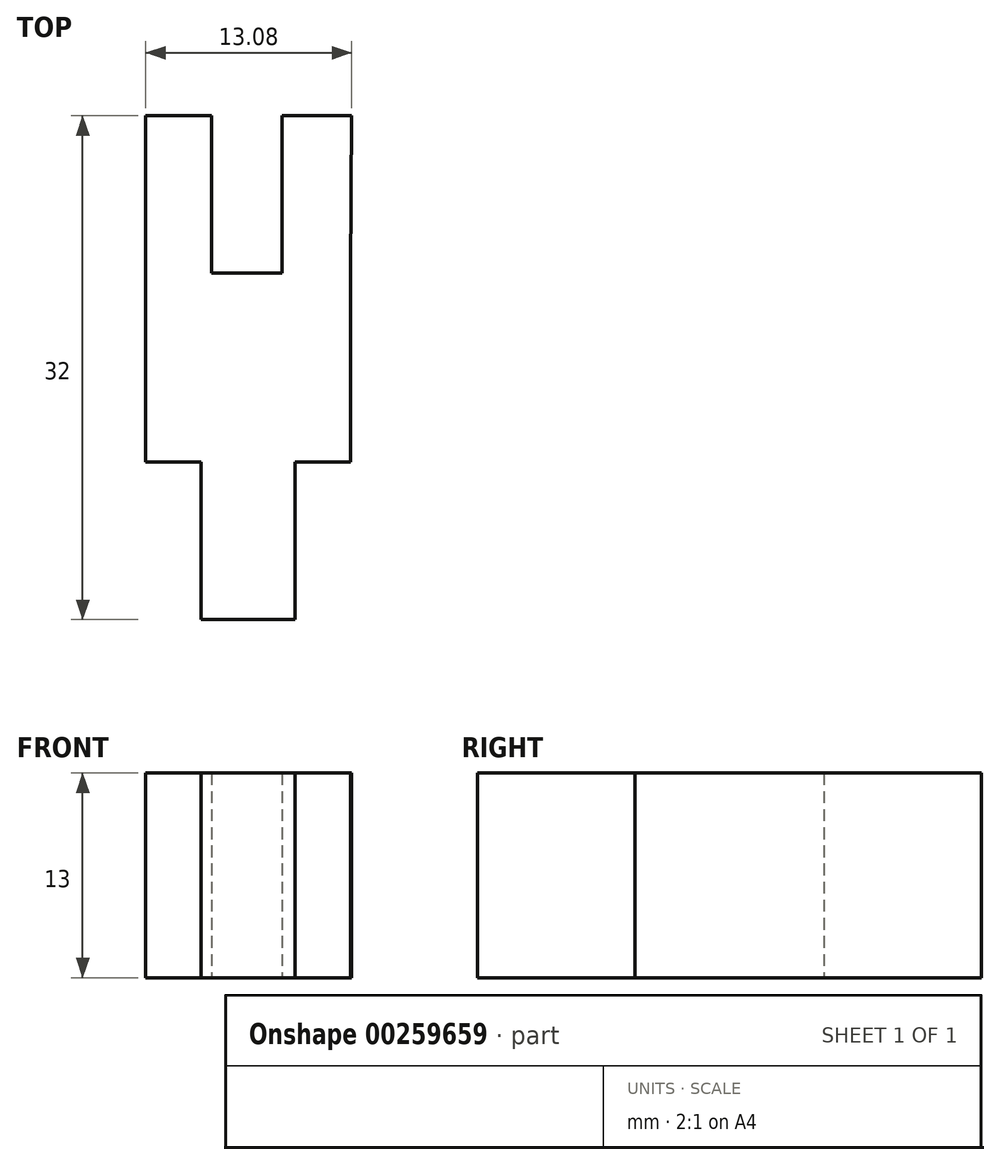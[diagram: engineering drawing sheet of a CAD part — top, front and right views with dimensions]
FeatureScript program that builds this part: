
annotation { "Feature Type Name" : "Feature", "Feature Type Description" : "" }
export const myFeature = defineFeature(function(context is Context, id is Id, definition is map)
    precondition{}
    {
        {
            var Q0;
            Q0=qCreatedBy(makeId("Top.planeOp"),FACE);
            var sketch = newSketch(context, id + "F0", { "sketchPlane" : qUnion([Q0])});
            skLineSegment(sketch, "E0.bottom", {"start": v(-43.6, -16.9) * mm, "end": v(-30.6, -16.9) * mm});
            skLineSegment(sketch, "E0.top", {"start": v(-43.6, -28.9) * mm, "end": v(-40.1, -28.9) * mm});
            skLineSegment(sketch, "E0.left", {"start": v(-43.6, -16.9) * mm, "end": v(-43.6, -28.9) * mm});
            skLineSegment(sketch, "E0.right", {"start": v(-30.6, -16.9) * mm, "end": v(-30.6, -28.9) * mm});
            skLineSegment(sketch, "E1", {"start": v(-43.6, -16.9) * mm, "end": v(-43.6, -6.9) * mm});
            skLineSegment(sketch, "E2", {"start": v(-43.6, -6.9) * mm, "end": v(-39.4, -6.9) * mm});
            skLineSegment(sketch, "E3", {"start": v(-39.4, -6.9) * mm, "end": v(-39.4, -16.9) * mm});
            skLineSegment(sketch, "E4", {"start": v(-39.4, -16.9) * mm, "end": v(-34.92, -16.9) * mm});
            skLineSegment(sketch, "E5", {"start": v(-34.92, -16.9) * mm, "end": v(-34.92, -6.9) * mm});
            skLineSegment(sketch, "E6", {"start": v(-34.92, -6.9) * mm, "end": v(-30.52, -6.9) * mm});
            skLineSegment(sketch, "E7", {"start": v(-30.52, -6.9) * mm, "end": v(-30.6, -16.9) * mm});
            skLineSegment(sketch, "E8", {"start": v(-40.1, -28.9) * mm, "end": v(-40.1, -38.9) * mm});
            skLineSegment(sketch, "E9", {"start": v(-40.1, -38.9) * mm, "end": v(-34.1, -38.9) * mm});
            skLineSegment(sketch, "E10", {"start": v(-34.1, -38.9) * mm, "end": v(-34.1, -28.9) * mm});
            skPoint(sketch, "E11", {"position": v(-43.6, -11.9) * mm});
            skPoint(sketch, "E12", {"position": v(-40.1, -33.9) * mm});
            skLineSegment(sketch, "E13.trimOffspring", {"start": v(-34.1, -28.9) * mm, "end": v(-30.6, -28.9) * mm});
            skSolve(sketch);
        }
        {
            var Q0;
            {var subQ0=sQuery(id+"F0.wireOp",EDGE,"E1");Q0=makeQuery(id+"F0.imprint","IMPRINT",FACE,{"disambiguationData":[TD([[makeQuery(id+"F0.imprint","IMPRINT",EDGE,{"derivedFrom":subQ0}),-1.0]])]});}
            var Q1;
            Q1=makeQuery(id+"F0.imprint","IMPRINT",FACE,{"disambiguationData":[TD([[makeQuery(id+"F0.imprint","IMPRINT",EDGE,{"derivedFrom":sQuery(id+"F0.wireOp",EDGE,"E0.top")}),1.0]])]});
            var Q2;
            {var subQ2=sQuery(id+"F0.wireOp",EDGE,"E5");Q2=makeQuery(id+"F0.imprint","IMPRINT",FACE,{"disambiguationData":[TD([[makeQuery(id+"F0.imprint","IMPRINT",EDGE,{"derivedFrom":subQ2}),-1.0]])]});}
            extrude(context, id + "F1", {"entities" : qUnion([Q0, Q1, Q2]), "depth" : 13 * mm});
        }
    });
